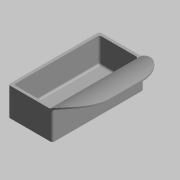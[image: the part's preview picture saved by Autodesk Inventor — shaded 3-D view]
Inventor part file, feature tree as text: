
AUTODESK INVENTOR PART (.ipt)
format: ipt  version: 2020 (Build 240168000, 168)  size: 162,304 bytes
history: native  units: mm (DEFAULTED — no unit token found)
features: extrude x3, sketch x3, fillet x2
ambient origin geometry x8: Origin, YZ Plane, XZ Plane, XY Plane, X Axis, Y Axis, Z Axis, Center Point
bodies: Solid1 (feature_tree)
feature tree (8):
  extrude  "Extrusion1"  Depth=97.0mm
  extrude  "Extrusion2"  Depth=48.5mm
  extrude  "Extrusion3"  Depth=32.0mm
  fillet  "Fillet2"  Radius=27.0mm
  fillet  "Fillet3"  Radius=30.0mm
  sketch  "Sketch1"  dims[d0=47.0mm d1=97.0mm]
  sketch  "Sketch2"  dims[d2=23.5mm d3=48.5mm]
  sketch  "Sketch4"  dims[d4=30.0mm d5=0.0mm d6=3.0mm d7=27.0mm d8=0.0mm d11=30.0mm d12=10.0mm d13=1.48221mm d14=10.0mm d15=0.0mm d16=2.0mm d17=32.0mm]
